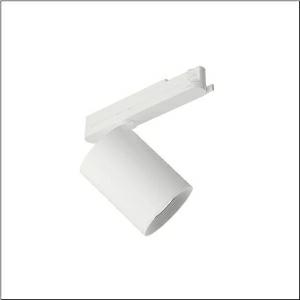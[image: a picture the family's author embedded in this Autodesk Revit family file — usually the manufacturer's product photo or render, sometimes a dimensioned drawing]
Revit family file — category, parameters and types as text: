
# Revit family: spot_11_51sd15mbd5a
name_source: partatom
category: Lighting Fixtures
units: mm (PartAtom-declared; Revit-internal decimal feet)

## family parameters
Cut with Voids When Loaded = No
Host = Face
Light Source = No
Part Type = Normal
Room Calculation Point = No
Round Connector Dimension = Use Diameter
Shared = No

## types (1)
- --- (1 x LED, 7520 lm, 50.9 W, 4000K)
    Apparent Load = 51 VA
    CIE Flux Codes = 91 98 100 100 100
    Color Rendering = 90
    Color Temperature = 4000K
    Default Elevation = 1800 mm
    Description = Spot 11, directional spotlight, light control with lens, of PMMA, LED rated luminous flux: 5.870lm, light colour: 940, control gear: ECG Multilumen, with 3-phase adapter, mains connection: 220..240V, AC, 50/60Hz, of aluminium, traffic white (RAL 9016), length: 213mm, diameter: 105mm, protection rating (complete): IP20, insulation class (complete): insulation class I (protective earthing), certification: CE, impact resistance: IK02, permissible ambient temperature for indoor applications: -20..+40°C, packaging unit: 1 piece
    Height = 175 mm
    Lamp = 1 x LED
    Lamp Light Flux = 7520 lm
    Lamp Power = 50.9 W
    Lamp count = 1
    Length = 105 mm
    Luminous efficacy = 148 lm/W
    Manufacturer = Siteco
    ModVariant = No
    Model = 51SD15MBD5A
    Mounting Place = Ceiling
    Mounting Type = Pendant
    Number of Poles = 1
    OnlyDefault = Yes
    Power Factor = 1
    Product Name = Spot 11
    Product group = directional spotlight
    ProductGroupID = 906
    Protection Class = Protection class I
    Protection Degree = IP 20
    RLX_Detail_Level = 1
    RLX_Emergency_Light_Flux = 0 lm
    RLX_Emergency_Type = 0
    RLX_Emergency_Type_DB = No
    RlxData = <blob elided: 17649 chars, md5=32e29f6b>
    Socket = socket
    Standby Power = 0 W
    System Light Flux = 7520 lm
    System Power = 51 W
    Type Comments = factory setting: luminous flux: 100 % | (ON | ON | ON | ON) | 1050 mA
    Type Image = l_1006697.jpg
    URL = http://relux.com
    VarID = @adj_146938
    Voltage = 0 V
    Weight = 0.00 kg
    Width = 0 mm  [stored 0 ft]

note: [stored X ft] marks values corroborated as IEEE doubles in the binary element streams (Revit-internal decimal feet)

## geometry (parser evidence)
native form markers: Blend x4, Sweep x10
no freeform markers — native parametric forms only
